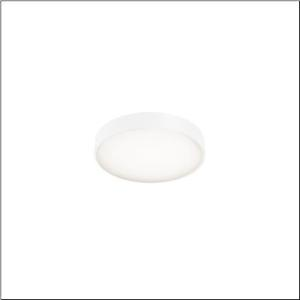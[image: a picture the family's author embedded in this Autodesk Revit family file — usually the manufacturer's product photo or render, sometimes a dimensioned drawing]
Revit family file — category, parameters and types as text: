
# Revit family: round_21_s_51mr34gd0321w
name_source: partatom
category: Lighting Fixtures
units: mm (PartAtom-declared; Revit-internal decimal feet)

## family parameters
Cut with Voids When Loaded = No
Host = Face
Light Source = No
Part Type = Normal
Room Calculation Point = No
Round Connector Dimension = Use Diameter
Shared = No

## types (1)
- Round 21 S (1 x LED, 3930 lm, 28.3 W, 3000K)
    Apparent Load = 28 VA
    CIE Flux Codes = 49 80 96 79 100
    Color Rendering = 80
    Color Temperature = 3000K
    Default Elevation = 1800 mm
    Description = Round 21 S, wall and ceiling luminaire, primary optical cover: cover, of PMMA, opal, light emission: direct/indirect distribution, primary light characteristic: symmetric, installation type: suspended mounting, surface-mounted, LED, rated luminous flux: 3.930lm, luminous efficacy: 139lm/W, light colour: 830, colour temperature: 3000K, control gear: DALI 2, with terminal, 5-pole, mains connection: 230V, AC, 50/60Hz, rated input power: 28.3W, housing, of aluminium, coated, white, diameter: 400mm, height: 62mm, protection rating (complete): IP40, insulation class (complete): insulation class I (protective earthing), certification: CE, impact resistance: IK04, permissible operating ambient temperature: -10..+35°C, packaging unit: 1 piece
    Height = 87 mm
    Lamp = 1 x LED
    Lamp Light Flux = 3930 lm
    Lamp Power = 28.3 W
    Lamp count = 1
    Length = 400 mm
    Luminous efficacy = 139 lm/W
    Manufacturer = Siteco
    ModVariant = No
    Model = 51MR34GD0321W
    Mounting Place = Wall
    Mounting Type = Surface mounted
    Number of Poles = 1
    OnlyDefault = Yes
    Power Factor = 1
    Product Name = Round 21 S
    Product group = wall and ceiling luminaire
    ProductGroupID = 2001
    Protection Class = Protection class I
    Protection Degree = IP 40
    RLX_Detail_Level = 1
    RLX_Emergency_Light_Flux = 0 lm
    RLX_Emergency_Type = 0
    RLX_Emergency_Type_DB = No
    RlxData = <blob elided: 9937 chars, md5=b70092d7>
    Socket = socket
    Standby Power = 0 W
    System Light Flux = 3930 lm
    System Power = 28 W
    Type Comments = Product without accessories
    Type Image = l_1258307.jpg
    URL = http://relux.com
    VarID = ---
    Voltage = 0 V
    Weight = 0.00 kg
    Width = 0 mm  [stored 0 ft]

note: [stored X ft] marks values corroborated as IEEE doubles in the binary element streams (Revit-internal decimal feet)

## geometry (parser evidence)
native form markers: Sweep x11
no freeform markers — native parametric forms only
